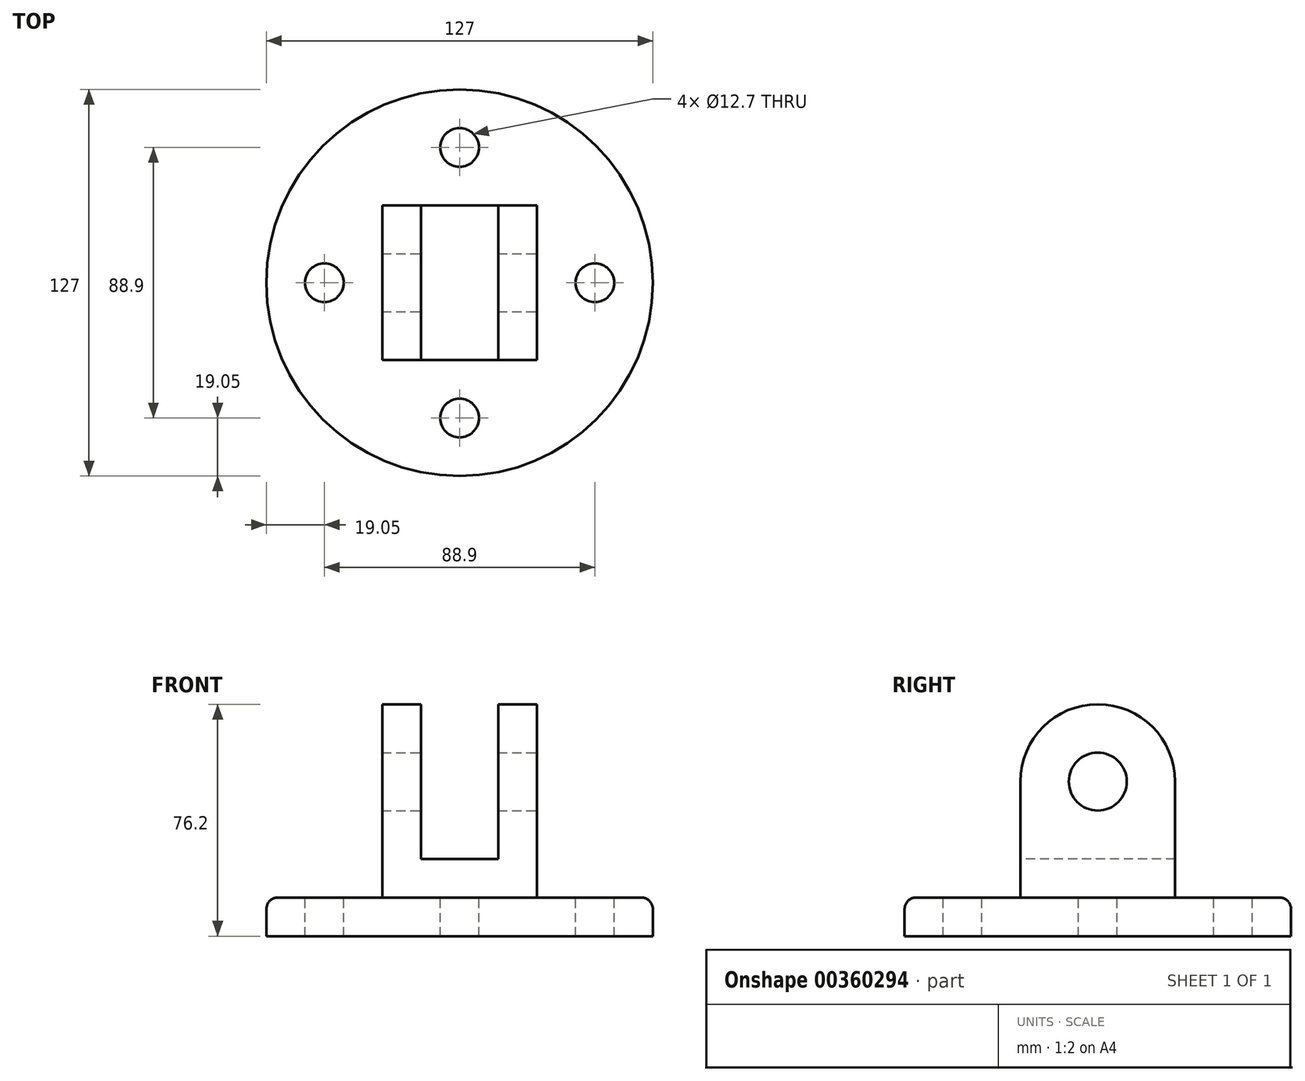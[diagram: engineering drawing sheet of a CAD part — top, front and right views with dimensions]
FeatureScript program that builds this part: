
annotation { "Feature Type Name" : "Feature", "Feature Type Description" : "" }
export const myFeature = defineFeature(function(context is Context, id is Id, definition is map)
    precondition{}
    {
        {
            var Q0;
            Q0=qCreatedBy(makeId("Top.planeOp"),FACE);
            var sketch = newSketch(context, id + "F0", { "sketchPlane" : qUnion([Q0])});
            skCircle(sketch, "E0", {"center": v(0, 0) * mm, "radius": 63.5 * mm});
            skSolve(sketch);
        }
        {
            var Q0;
            Q0 = qSketchRegion(id + "F0", true);
            extrude(context, id + "F1", {"entities" : qUnion([Q0]), "depth" : 12.7 * mm});
        }
        {
            var Q0;
            Q0=makeQuery(id+"F1.opExtrude","CAP_FACE",FACE,{"disambiguationData":[OSD([sQuery(id+"F0.wireOp",EDGE,"E0")])],"isStart":false});
            var sketch = newSketch(context, id + "F2", { "sketchPlane" : qUnion([Q0])});
            skLineSegment(sketch, "E1", {"start": v(0, 75.34) * mm, "end": v(0, -75.61) * mm, "construction": true});
            skLineSegment(sketch, "E2", {"start": v(-76.3, 0) * mm, "end": v(76.3, 0) * mm, "construction": true});
            skCircle(sketch, "E3", {"center": v(0, 44.45) * mm, "radius": 6.35 * mm});
            skCircle(sketch, "E4", {"center": v(0, -44.45) * mm, "radius": 6.35 * mm});
            skCircle(sketch, "E5", {"center": v(44.45, 0) * mm, "radius": 6.35 * mm});
            skCircle(sketch, "E6", {"center": v(-44.45, 0) * mm, "radius": 6.35 * mm});
            skLineSegment(sketch, "E7.bottom", {"start": v(-25.4, 25.4) * mm, "end": v(25.4, 25.4) * mm});
            skLineSegment(sketch, "E7.top", {"start": v(-25.4, -25.4) * mm, "end": v(25.4, -25.4) * mm});
            skLineSegment(sketch, "E7.left", {"start": v(-25.4, 25.4) * mm, "end": v(-25.4, -25.4) * mm});
            skLineSegment(sketch, "E7.right", {"start": v(25.4, 25.4) * mm, "end": v(25.4, -25.4) * mm});
            skCircle(sketch, "E8", {"center": v(0, 0) * mm, "radius": 44.45 * mm, "construction": true});
            skSolve(sketch);
        }
        {
            var Q0;
            Q0=makeQuery(id+"F2.imprint","IMPRINT",FACE,{"disambiguationData":[TD([[makeQuery(id+"F2.imprint","IMPRINT",EDGE,{"derivedFrom":sQuery(id+"F2.wireOp",EDGE,"E7.bottom")}),-1.0]])]});
            extrude(context, id + "F3", {"entities" : qUnion([Q0]), "operationType" : NewBodyOperationType.ADD, "depth" : 38.1 * mm});
        }
        {
            var Q0;
            Q0=makeQuery(id+"F2.imprint","IMPRINT",FACE,{"disambiguationData":[TD([[makeQuery(id+"F2.imprint","IMPRINT",EDGE,{"derivedFrom":sQuery(id+"F2.wireOp",EDGE,"E5")}),1.0]])]});
            var Q1;
            Q1=makeQuery(id+"F2.imprint","IMPRINT",FACE,{"disambiguationData":[TD([[makeQuery(id+"F2.imprint","IMPRINT",EDGE,{"derivedFrom":sQuery(id+"F2.wireOp",EDGE,"E6")}),1.0]])]});
            var Q2;
            Q2=makeQuery(id+"F2.imprint","IMPRINT",FACE,{"disambiguationData":[TD([[makeQuery(id+"F2.imprint","IMPRINT",EDGE,{"derivedFrom":sQuery(id+"F2.wireOp",EDGE,"E3")}),1.0]])]});
            var Q3;
            Q3=makeQuery(id+"F2.imprint","IMPRINT",FACE,{"disambiguationData":[TD([[makeQuery(id+"F2.imprint","IMPRINT",EDGE,{"derivedFrom":sQuery(id+"F2.wireOp",EDGE,"E4")}),1.0]])]});
            extrude(context, id + "F4", {"entities" : qUnion([Q0, Q1, Q2, Q3]), "operationType" : NewBodyOperationType.REMOVE, "oppositeDirection" : true, "depth" : 25.4 * mm});
        }
        {
            var Q0;
            Q0=makeQuery(id+"F3.opExtrude","SWEPT_FACE",FACE,{"disambiguationData":[OSD([sQuery(id+"F2.wireOp",EDGE,"E7.top")])]});
            var sketch = newSketch(context, id + "F5", { "sketchPlane" : qUnion([Q0])});
            skLineSegment(sketch, "E9.bottom", {"start": v(-12.7, 50.8) * mm, "end": v(12.7, 50.8) * mm});
            skLineSegment(sketch, "E9.top", {"start": v(-12.7, 25.4) * mm, "end": v(12.7, 25.4) * mm});
            skLineSegment(sketch, "E9.left", {"start": v(-12.7, 50.8) * mm, "end": v(-12.7, 25.4) * mm});
            skLineSegment(sketch, "E9.right", {"start": v(12.7, 50.8) * mm, "end": v(12.7, 25.4) * mm});
            skSolve(sketch);
        }
        {
            var Q0;
            Q0 = qSketchRegion(id + "F5", true);
            extrude(context, id + "F6", {"entities" : qUnion([Q0]), "operationType" : NewBodyOperationType.REMOVE, "endBound" : BoundingType.THROUGH_ALL, "oppositeDirection" : true, "depth" : 25.4 * mm});
        }
        {
            var Q0;
            Q0=makeQuery(id+"F3.opExtrude","SWEPT_FACE",FACE,{"disambiguationData":[OSD([sQuery(id+"F2.wireOp",EDGE,"E7.right")])]});
            var sketch = newSketch(context, id + "F7", { "sketchPlane" : qUnion([Q0])});
            skArc(sketch, "E10", {"start": v(25.4, 50.8) * mm, "mid": v(0, 76.2) * mm, "end": v(-25.4, 50.8) * mm});
            skLineSegment(sketch, "E11", {"start": v(-25.4, 50.8) * mm, "end": v(-9.52, 50.8) * mm});
            skCircle(sketch, "E12", {"center": v(0, 50.8) * mm, "radius": 9.53 * mm});
            skLineSegment(sketch, "E13.trimOffspring", {"start": v(9.52, 50.8) * mm, "end": v(25.4, 50.8) * mm});
            skSolve(sketch);
        }
        {
            var Q0;
            Q0 = qSketchRegion(id + "F7", true);
            var Q1;
            {var subQ0=sQuery(id+"F2.wireOp",EDGE,"E7.bottom");var subQ1=sQuery(id+"F2.wireOp",EDGE,"E7.right");var subQ2=sQuery(id+"F2.wireOp",EDGE,"E7.top");Q1=makeQuery(id+"F6.boolean.opBoolean","SPLIT",FACE,{"disambiguationData":[TD([makeQuery(id+"F3.opExtrude","SWEPT_FACE",FACE,{"disambiguationData":[OSD([subQ1])]})])],"derivedFrom":makeQuery(id+"F3.opExtrude","CAP_FACE",FACE,{"disambiguationData":[OSD([subQ0,subQ2,sQuery(id+"F2.wireOp",EDGE,"E7.left"),subQ1])],"isStart":false})});}
            extrude(context, id + "F8", {"entities" : qUnion([Q0]), "operationType" : NewBodyOperationType.ADD, "oppositeDirection" : true, "endBoundEntityFace" : qUnion([Q1]), "depth" : 12.7 * mm});
        }
        {
            var Q0;
            Q0=makeQuery(id+"F3.opExtrude","SWEPT_FACE",FACE,{"disambiguationData":[OSD([sQuery(id+"F2.wireOp",EDGE,"E7.left")])]});
            var sketch = newSketch(context, id + "F9", { "sketchPlane" : qUnion([Q0])});
            skArc(sketch, "E14", {"start": v(25.4, 50.8) * mm, "mid": v(0, 76.2) * mm, "end": v(-25.4, 50.8) * mm});
            skLineSegment(sketch, "E15", {"start": v(-25.4, 50.8) * mm, "end": v(25.4, 50.8) * mm});
            skSolve(sketch);
        }
        {
            var Q0;
            Q0 = qSketchRegion(id + "F9", true);
            extrude(context, id + "F10", {"entities" : qUnion([Q0]), "operationType" : NewBodyOperationType.ADD, "oppositeDirection" : true, "depth" : 12.7 * mm});
        }
        {
            var Q0;
            {var subQ0=sQuery(id+"F7.wireOp",EDGE,"E12");var subQ1=makeQuery(id+"F3.opExtrude","CAP_EDGE",EDGE,{"disambiguationData":[OSD([sQuery(id+"F2.wireOp",EDGE,"E7.right")])],"isStart":false});var subQ2=makeQuery(id+"F7.imprint","INTERSECT",VERTEX,{"derivedFrom":[subQ1,sQuery(id+"F7.wireOp",EDGE,"E11"),subQ0]});Q0=makeQuery(id+"F7.imprint","IMPRINT",FACE,{"disambiguationData":[TD([[makeQuery(id+"F7.imprint","IMPRINT",EDGE,{"disambiguationData":[TD([[subQ2,1.0]])],"derivedFrom":subQ0}),1.0]])]});}
            var Q1;
            {var subQ0=sQuery(id+"F7.wireOp",EDGE,"E12");var subQ1=makeQuery(id+"F3.opExtrude","CAP_EDGE",EDGE,{"disambiguationData":[OSD([sQuery(id+"F2.wireOp",EDGE,"E7.right")])],"isStart":false});var subQ2=makeQuery(id+"F7.imprint","INTERSECT",VERTEX,{"derivedFrom":[subQ1,sQuery(id+"F7.wireOp",EDGE,"E11"),subQ0]});Q1=makeQuery(id+"F7.imprint","IMPRINT",FACE,{"disambiguationData":[TD([[makeQuery(id+"F7.imprint","IMPRINT",EDGE,{"disambiguationData":[TD([[subQ2,-1.0]])],"derivedFrom":subQ0}),1.0]])]});}
            extrude(context, id + "F11", {"entities" : qUnion([Q0, Q1]), "operationType" : NewBodyOperationType.REMOVE, "endBound" : BoundingType.THROUGH_ALL, "oppositeDirection" : true, "depth" : 25.4 * mm});
        }
        {
            var Q0;
            Q0=makeQuery(id+"F1.opExtrude","CAP_EDGE",EDGE,{"disambiguationData":[OSD([sQuery(id+"F0.wireOp",EDGE,"E0")])],"isStart":false});
            var Q1;
            Q1=makeQuery(id+"F3.opExtrude","CAP_EDGE",EDGE,{"disambiguationData":[OSD([sQuery(id+"F2.wireOp",EDGE,"E7.top")])],"isStart":true});
            var Q2;
            Q2=makeQuery(id+"F3.opExtrude","CAP_EDGE",EDGE,{"disambiguationData":[OSD([sQuery(id+"F2.wireOp",EDGE,"E7.right")])],"isStart":true});
            var Q3;
            Q3=makeQuery(id+"F3.opExtrude","CAP_EDGE",EDGE,{"disambiguationData":[OSD([sQuery(id+"F2.wireOp",EDGE,"E7.bottom")])],"isStart":true});
            var Q4;
            Q4=makeQuery(id+"F3.opExtrude","CAP_EDGE",EDGE,{"disambiguationData":[OSD([sQuery(id+"F2.wireOp",EDGE,"E7.left")])],"isStart":true});
            fillet(context, id + "F12", {"entities" : qUnion([Q0, Q1, Q2, Q3, Q4]), "radius" : 3.8 * mm, "tangentPropagation" : true, "allowEdgeOverflow" : false});
        }
    });
